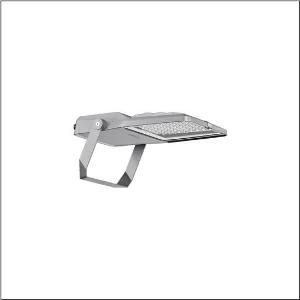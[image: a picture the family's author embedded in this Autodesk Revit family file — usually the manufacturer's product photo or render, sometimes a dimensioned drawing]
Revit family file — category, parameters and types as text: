
# Revit family: floodlight_fl_21_iq_mini___pl43_5xa7771b4a1a_3306
name_source: partatom
category: Lighting Fixtures
units: mm (PartAtom-declared; Revit-internal decimal feet)

## family parameters
Cut with Voids When Loaded = No
Host = Face
Light Source = No
Part Type = Normal
Room Calculation Point = No
Round Connector Dimension = Use Diameter
Shared = No

## types (1)
- --- (1 x LED, 6660 lm, 45.5 W, 4000K)
    Apparent Load = 46 VA
    CIE Flux Codes = 27 78 99 100 100
    Color Rendering = 70
    Color Temperature = 4000K
    Default Elevation = 1800 mm
    Description = Floodlight FL 21 iQ mini, floodlight, primary light control with lens, of PMMA, primary optical cover: protective disc, of toughened safety glass, transparent, light distribution: PL43, light emission: direct distribution, installation type: surface-mounted, lamps: LED, High Power LED, rated values: 6.660lm | 45,5W | 146,4lm/W (begin service life); end service life: 6.660lm | 48W; at 50% lumin. flux: 3.330lm | 21,5W | 154,9lm/W, colour temperature: 4000K, colour rendering: CRI > 70, light colour: 740, light setting 1 begin service life: 100% | 6.660lm | 45,5W | 146,4lm/W | 4.000K, light setting 1 end service life: 48W, further light settings possible, control: Auto-Match, Temp-Guard, Lumen-Switch, Night-Set, Smart-Wire, Light-Fading, Desk-Remote (wireless, voltage-free reading and setting of iQ features in the workshop via application-optimized NFC function/RFID function), optimised constant luminous flux control (CLO 2.0), pre-setting: linear dimming characteristic, with terminal, 6-pole, mains connection: 220..240V, AC, 50/60Hz, luminaire housing, of diecast aluminium, powder-coated, SITECO metallic grey (DB 702S), corrosivity category C5 mid according to DIN EN ISO 12944suitable for swimming poolschlorine-resistant, sealing non-destructively replaceable, mounting bracket, of steel, galvanised, powder-coated, SITECO metallic grey (DB 702S), protection rating (complete): IP66, insulation class (complete): insulation class II (safety insulation), certification: CE, ENEC, VDE, protection symbol: D, impact resistance: IK08, permissible operating ambient temperature: -40..+40°C, permissible operating ambient temperature for outdoor applications: -40..+50°C, standard: DIN EN 12944, LABS conformity tested according to VDMA 24364:2018-05, packaging unit: 1 piece

Light Distribution: PL43
    Height = 70 mm
    Lamp = 1 x LED
    Lamp Light Flux = 6660 lm
    Lamp Power = 45.5 W
    Lamp count = 1
    Length = 485 mm
    Luminous efficacy = 146 lm/W
    Manufacturer = Siteco
    ModVariant = No
    Model = 5XA7771B4A1A
    Mounting Place = Wall
    Mounting Type = Surface mounted
    Number of Poles = 1
    OnlyDefault = Yes
    Power Factor = 1
    Product Name = Floodlight FL 21 iQ mini | PL43
    Product group = floodlight | wall mounted
    ProductGroupID = 2002
    Protection Class = Protection class II
    Protection Degree = IP 66
    RLX_Detail_Level = 1
    RLX_Emergency_Light_Flux = 0 lm
    RLX_Emergency_Type = 0
    RLX_Emergency_Type_DB = No
    RlxData = <blob elided: 96369 chars, md5=dacea68b>
    Socket = socket
    Standby Power = 0 W
    System Light Flux = 6660 lm
    System Power = 46 W
    Type Comments = factory setting: luminous flux: 100 % | dim-lin: 254 | 463 mA
    Type Image = l_1006845.jpg
    URL = http://relux.com
    VarID = @adj_163031
    Voltage = 0 V
    Weight = 0.00 kg
    Width = 337 mm

## geometry (parser evidence)
native form markers: Blend x4, Sweep x11
no freeform markers — native parametric forms only
